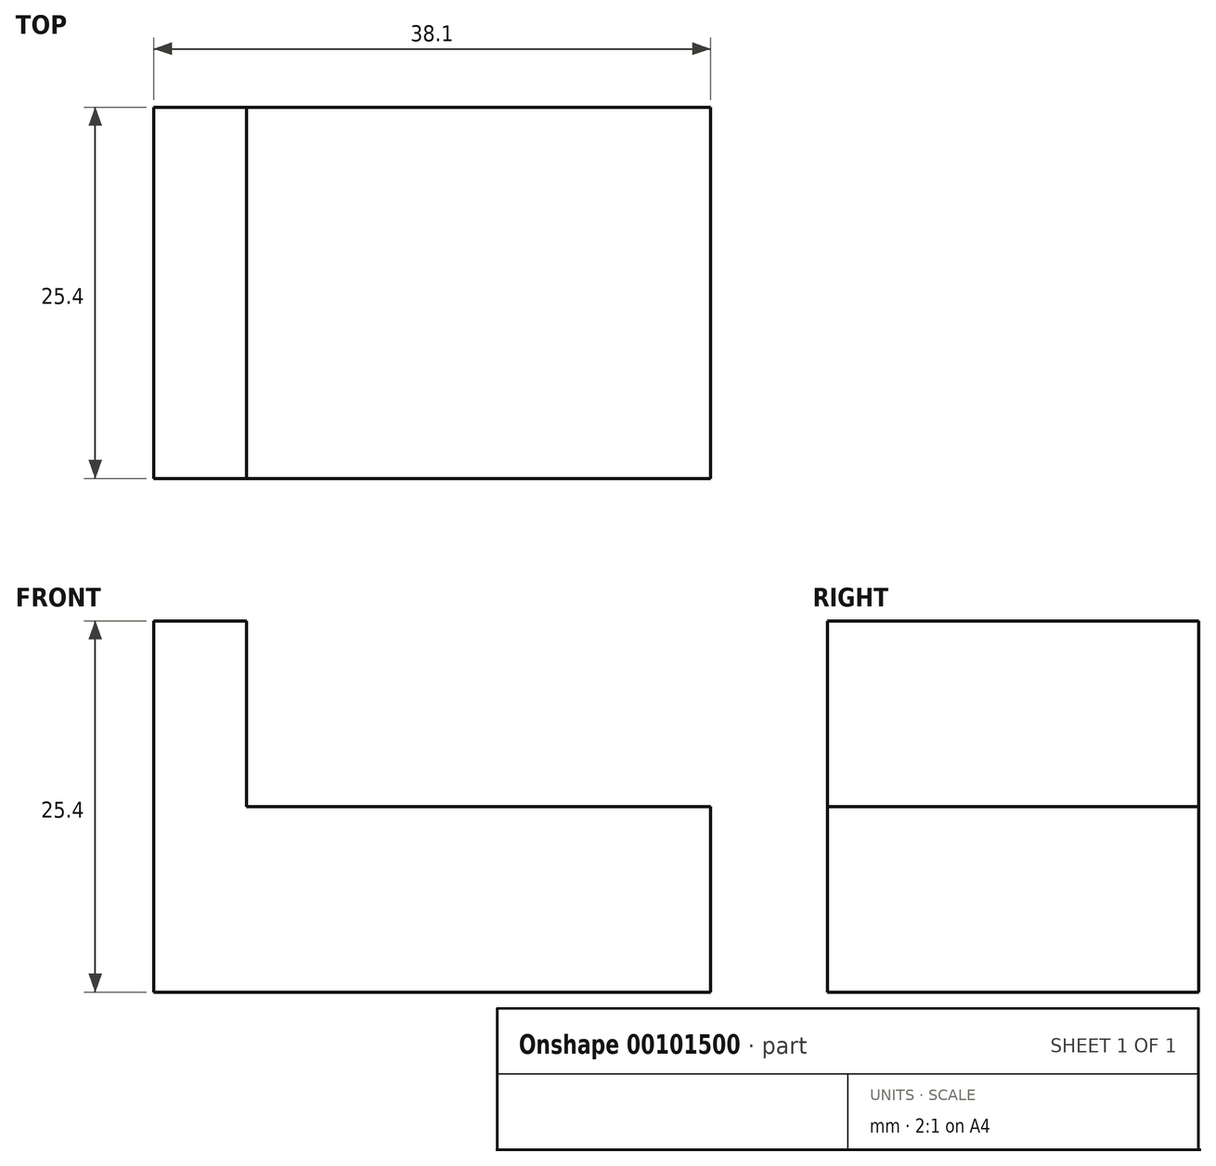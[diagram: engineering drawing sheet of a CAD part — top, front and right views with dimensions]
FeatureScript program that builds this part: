
annotation { "Feature Type Name" : "Feature", "Feature Type Description" : "" }
export const myFeature = defineFeature(function(context is Context, id is Id, definition is map)
    precondition{}
    {
        {
            var Q0;
            Q0=qCreatedBy(makeId("Front.planeOp"),FACE);
            var sketch = newSketch(context, id + "F0", { "sketchPlane" : qUnion([Q0])});
            skLineSegment(sketch, "E0", {"start": v(0, 25.4) * mm, "end": v(6.35, 25.4) * mm});
            skLineSegment(sketch, "E1", {"start": v(6.35, 25.4) * mm, "end": v(6.35, 12.7) * mm});
            skLineSegment(sketch, "E2", {"start": v(6.35, 12.7) * mm, "end": v(38.1, 12.7) * mm});
            skLineSegment(sketch, "E3", {"start": v(38.1, 12.7) * mm, "end": v(38.1, 0) * mm});
            skLineSegment(sketch, "E4", {"start": v(38.1, 0) * mm, "end": v(0, 0) * mm});
            skLineSegment(sketch, "E5", {"start": v(0, 0) * mm, "end": v(0, 25.4) * mm});
            skSolve(sketch);
        }
        {
            var Q0;
            Q0 = qSketchRegion(id + "F0", true);
            extrude(context, id + "F1", {"entities" : qUnion([Q0]), "oppositeDirection" : true, "depth" : 25.4 * mm});
        }
    });
